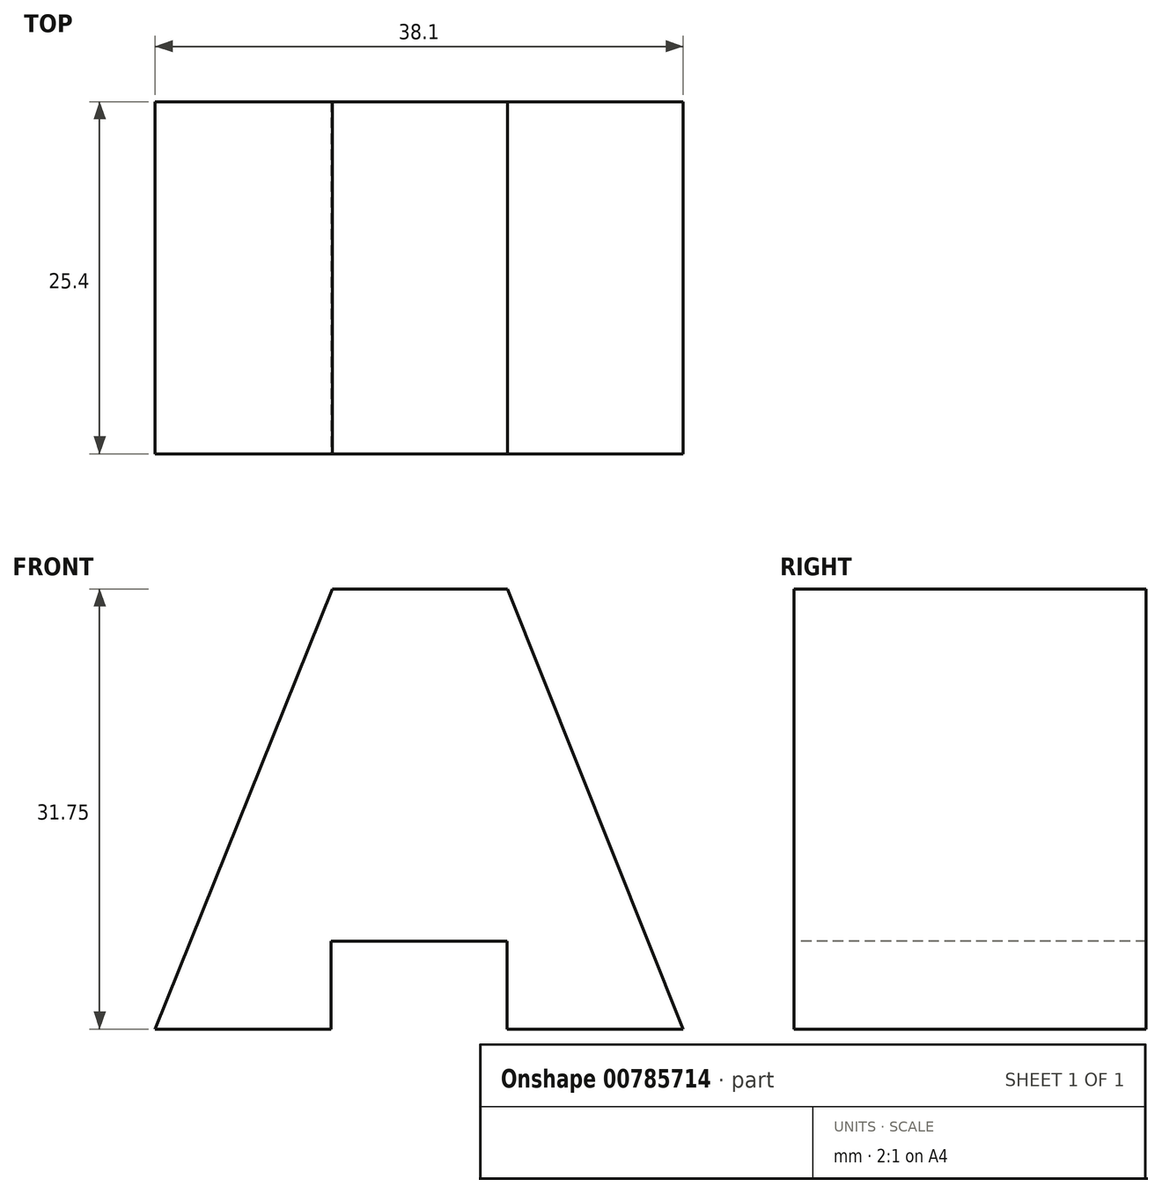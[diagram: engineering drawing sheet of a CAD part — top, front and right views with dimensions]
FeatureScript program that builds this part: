
annotation { "Feature Type Name" : "Feature", "Feature Type Description" : "" }
export const myFeature = defineFeature(function(context is Context, id is Id, definition is map)
    precondition{}
    {
        {
            var Q0;
            Q0=qCreatedBy(makeId("Front.planeOp"),FACE);
            var sketch = newSketch(context, id + "F0", { "sketchPlane" : qUnion([Q0])});
            skLineSegment(sketch, "E0", {"start": v(0, 0) * mm, "end": v(38.1, 0) * mm});
            skLineSegment(sketch, "E1", {"start": v(38.1, 0) * mm, "end": v(38.1, 31.75) * mm});
            skLineSegment(sketch, "E2", {"start": v(38.1, 31.75) * mm, "end": v(0, 31.75) * mm});
            skLineSegment(sketch, "E3", {"start": v(0, 31.75) * mm, "end": v(0, 0) * mm});
            skSolve(sketch);
        }
        {
            var Q0;
            Q0=qCreatedBy(makeId("Front.planeOp"),FACE);
            var sketch = newSketch(context, id + "F1", { "sketchPlane" : qUnion([Q0])});
            skSolve(sketch);
        }
        {
            var Q0;
            Q0 = qSketchRegion(id + "F1", true);
            var Q1;
            Q1=makeQuery(id+"F0.imprint","IMPRINT",FACE,{"disambiguationData":[TD([[makeQuery(id+"F0.imprint","IMPRINT",EDGE,{"derivedFrom":sQuery(id+"F0.wireOp",EDGE,"E0")}),1.0]])]});
            extrude(context, id + "F2", {"entities" : qUnion([Q0, Q1]), "depth" : 25.4 * mm, "offsetDistance" : 25.4 * mm});
        }
        {
            var Q0;
            Q0=qCreatedBy(makeId("Front.planeOp"),FACE);
            var sketch = newSketch(context, id + "F3", { "sketchPlane" : qUnion([Q0])});
            skLineSegment(sketch, "E4", {"start": v(12.77, 31.57) * mm, "end": v(0, 0) * mm});
            skSolve(sketch);
        }
        {
            var Q0;
            Q0=qCreatedBy(makeId("Front.planeOp"),FACE);
            var sketch = newSketch(context, id + "F4", { "sketchPlane" : qUnion([Q0])});
            skLineSegment(sketch, "E5", {"start": v(25.22, 31.84) * mm, "end": v(38.2, 0) * mm});
            skSolve(sketch);
        }
        {
            var Q0;
            Q0=qCreatedBy(makeId("Front.planeOp"),FACE);
            var sketch = newSketch(context, id + "F5", { "sketchPlane" : qUnion([Q0])});
            skLineSegment(sketch, "E6", {"start": v(12.23, 0) * mm, "end": v(12.23, 6.35) * mm});
            skLineSegment(sketch, "E7", {"start": v(12.23, 6.35) * mm, "end": v(24.93, 6.35) * mm});
            skLineSegment(sketch, "E8", {"start": v(24.93, 6.35) * mm, "end": v(24.93, 0) * mm});
            skSolve(sketch);
        }
        {
            var Q0;
            Q0=sQuery(id+"F3.wireOp",EDGE,"E4");
            var Q1;
            Q1=sQuery(id+"F4.wireOp",EDGE,"E5");
            var Q2;
            Q2=sQuery(id+"F5.wireOp",EDGE,"E7");
            extrude(context, id + "F6", {"bodyType" : ToolBodyType.SURFACE, "surfaceEntities" : qUnion([Q0, Q1, Q2]), "depth" : 25.4 * mm, "offsetDistance" : 25.4 * mm});
        }
        {
            var Q0;
            Q0=makeQuery(id+"F2.opExtrude","CAP_FACE",FACE,{"disambiguationData":[OSD([sQuery(id+"F0.wireOp",EDGE,"E0"),sQuery(id+"F0.wireOp",EDGE,"E1"),sQuery(id+"F0.wireOp",EDGE,"E2"),sQuery(id+"F0.wireOp",EDGE,"E3")])],"isStart":false});
            var sketch = newSketch(context, id + "F7", { "sketchPlane" : qUnion([Q0])});
            skLineSegment(sketch, "E9", {"start": v(0, 0) * mm, "end": v(12.7, 0) * mm});
            skLineSegment(sketch, "E10", {"start": v(12.7, 0) * mm, "end": v(12.7, 6.35) * mm});
            skLineSegment(sketch, "E11", {"start": v(12.7, 6.35) * mm, "end": v(25.4, 6.35) * mm});
            skLineSegment(sketch, "E12", {"start": v(25.4, 6.35) * mm, "end": v(25.4, 0) * mm});
            skLineSegment(sketch, "E13", {"start": v(25.4, 0) * mm, "end": v(38.1, 0) * mm});
            skSolve(sketch);
        }
        {
            var Q0;
            {var subQ0=sQuery(id+"F7.wireOp",EDGE,"E10");Q0=makeQuery(id+"F7.imprint","IMPRINT",FACE,{"disambiguationData":[TD([[makeQuery(id+"F7.imprint","IMPRINT",EDGE,{"derivedFrom":subQ0}),-1.0]])]});}
            extrude(context, id + "F8", {"entities" : qUnion([Q0]), "operationType" : NewBodyOperationType.REMOVE, "oppositeDirection" : true, "depth" : 25.4 * mm, "offsetDistance" : 25.4 * mm});
        }
        {
            var Q0;
            Q0=makeQuery(id+"F2.opExtrude","CAP_FACE",FACE,{"disambiguationData":[OSD([sQuery(id+"F0.wireOp",EDGE,"E0"),sQuery(id+"F0.wireOp",EDGE,"E1"),sQuery(id+"F0.wireOp",EDGE,"E2"),sQuery(id+"F0.wireOp",EDGE,"E3")])],"isStart":false});
            var sketch = newSketch(context, id + "F9", { "sketchPlane" : qUnion([Q0])});
            skLineSegment(sketch, "E14", {"start": v(0, 0) * mm, "end": v(12.77, 31.75) * mm});
            skLineSegment(sketch, "E15", {"start": v(12.77, 31.75) * mm, "end": v(25.47, 31.75) * mm});
            skLineSegment(sketch, "E16", {"start": v(25.47, 31.75) * mm, "end": v(38.1, 0) * mm});
            skSolve(sketch);
        }
        {
            var Q0;
            {var subQ0=sQuery(id+"F9.wireOp",EDGE,"E14");Q0=makeQuery(id+"F9.imprint","IMPRINT",FACE,{"disambiguationData":[TD([[makeQuery(id+"F9.imprint","IMPRINT",EDGE,{"derivedFrom":subQ0}),1.0]])]});}
            extrude(context, id + "F10", {"entities" : qUnion([Q0]), "operationType" : NewBodyOperationType.REMOVE, "oppositeDirection" : true, "depth" : 25.4 * mm, "offsetDistance" : 25.4 * mm});
        }
        {
            var Q0;
            Q0=makeQuery(id+"F2.opExtrude","CAP_FACE",FACE,{"disambiguationData":[OSD([sQuery(id+"F0.wireOp",EDGE,"E0"),sQuery(id+"F0.wireOp",EDGE,"E1"),sQuery(id+"F0.wireOp",EDGE,"E2"),sQuery(id+"F0.wireOp",EDGE,"E3")])],"isStart":false});
            var sketch = newSketch(context, id + "F11", { "sketchPlane" : qUnion([Q0])});
            skLineSegment(sketch, "E17", {"start": v(38.1, 0) * mm, "end": v(25.44, 31.75) * mm});
            skSolve(sketch);
        }
        {
            var Q0;
            {var subQ0=sQuery(id+"F11.wireOp",EDGE,"E17");Q0=makeQuery(id+"F11.imprint","IMPRINT",FACE,{"disambiguationData":[TD([[makeQuery(id+"F11.imprint","IMPRINT",EDGE,{"derivedFrom":subQ0}),-1.0]])]});}
            extrude(context, id + "F12", {"entities" : qUnion([Q0]), "operationType" : NewBodyOperationType.REMOVE, "oppositeDirection" : true, "depth" : 25.4 * mm, "offsetDistance" : 25.4 * mm});
        }
    });
